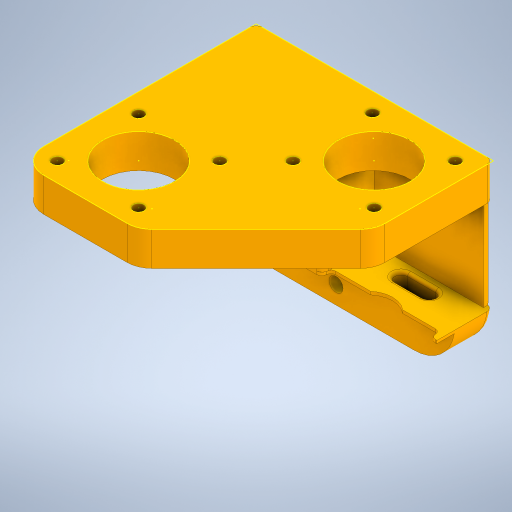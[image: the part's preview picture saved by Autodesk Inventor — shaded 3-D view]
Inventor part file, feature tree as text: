
AUTODESK INVENTOR PART (.ipt)
format: ipt  version: 2024 (Build 280153000, 153)  size: 664,576 bytes
history: native  units: mm
features: sketch x12, extrude x10, fillet x9, projected_geometry x3, hole x1
ambient origin geometry x8: Origin, YZ Plane, XZ Plane, XY Plane, X Axis, Y Axis, Z Axis, Center Point
bodies: Solid1 (feature_tree)
feature tree (35):
  sketch  "Sketch1"  dims[d0=35.3mm d1=35.3mm]
  extrude  "Extrusion1"  Depth=35.3mm
  extrude  "Extrusion2"  Depth=35.3mm
  fillet  "Fillet1"  Radius=26.0mm
  fillet  "Fillet3"  Radius=26.0mm
  extrude  "Extrusion3"  Depth=3.5mm
  hole  "Hole1"  [1 undecoded]
  extrude  "Extrusion4"  Depth=3.5mm
  extrude  "Extrusion5"  Depth=3.5mm
  fillet  "Fillet5"  Radius=3.5mm
  fillet  "Fillet6"  Radius=23.0mm
  extrude  "Extrusion6"  Depth=10.875mm TaperAngle=0.0deg
  fillet  "Fillet7"  Radius=30.0mm
  fillet  "Fillet8"  Radius=20.0mm
  extrude  "Extrusion7"  Depth=2.0mm TaperAngle=0.0deg
  fillet  "Fillet9"  Radius=12.0mm
  fillet  "Fillet10"  Radius=3.0mm
  sketch  "Sketch15"  dims[d24=2.0mm d25=12.0mm d26=0.0mm]
  sketch  "Sketch26"  dims[d27=4.5mm d28=9.0mm d29=5.5mm d30=2.0mm d31=90.0deg d32=13.0mm d33=0.0mm d35=12.0mm d36=0.0mm d37=3.0mm d38=0.0mm]
  extrude  "Extrusion34"  Depth=13.0mm
  fillet  "Fillet34"  Radius=2.0mm
  extrude  "Extrusion44"  Depth=8.0mm
  extrude  "Extrusion45"  Depth=2.0mm
  sketch  "Sketch3"  dims[d2=35.3mm d3=35.3mm d4=26.0mm d6=26.0mm]
  sketch  "Sketch4"  dims[d7=26.0mm d8=3.5mm]
  sketch  "Sketch6"  dims[d9=3.5mm d10=3.5mm]
  sketch  "Sketch7"  dims[d11=3.5mm d12=3.5mm]
  sketch  "Sketch8"  dims[d13=3.5mm d14=3.5mm d15=3.5mm d16=23.0mm]
  sketch  "Sketch10"  dims[d17=23.0mm d18=10.875mm d19=0.0mm d20=30.0mm d21=0.0mm d22=20.0mm]
  projected_geometry  "Projected Loop3"
  projected_geometry  "Projected Loop13"
  sketch  "Sketch37"  dims[d39=1.5mm d40=13.0mm d41=2.0mm d42=0.0mm]
  projected_geometry  "Projected Loop19"
  sketch  "Sketch47"  dims[d43=8.0mm d53=8.0mm]
  sketch  "Sketch48"  dims[d54=33.0mm d55=0.0mm d56=1.0mm d57=1.0mm d58=6.25mm d59=38.0mm d60=38.0mm d147=26.0mm d148=6.096mm d149=6.096mm d150=13.0mm d151=13.0mm d198=6.0mm d199=6.0mm d200=6.0mm d201=6.0mm d202=6.0mm d203=6.0mm d204=6.0mm d205=6.0mm d206=10.0mm d207=0.0mm d241=2.0mm d269=3.5mm d270=3.5mm d271=10.875mm d272=0.0mm d273=26.25mm d274=0.0mm d266=0.5mm d267=0.872665mm d268=0.5mm]
note: 1 required parameter value undecoded (feature->parameter linkage not recoverable at this tier; creation-order binding heuristic only, values carry confidence <= 0.55)
